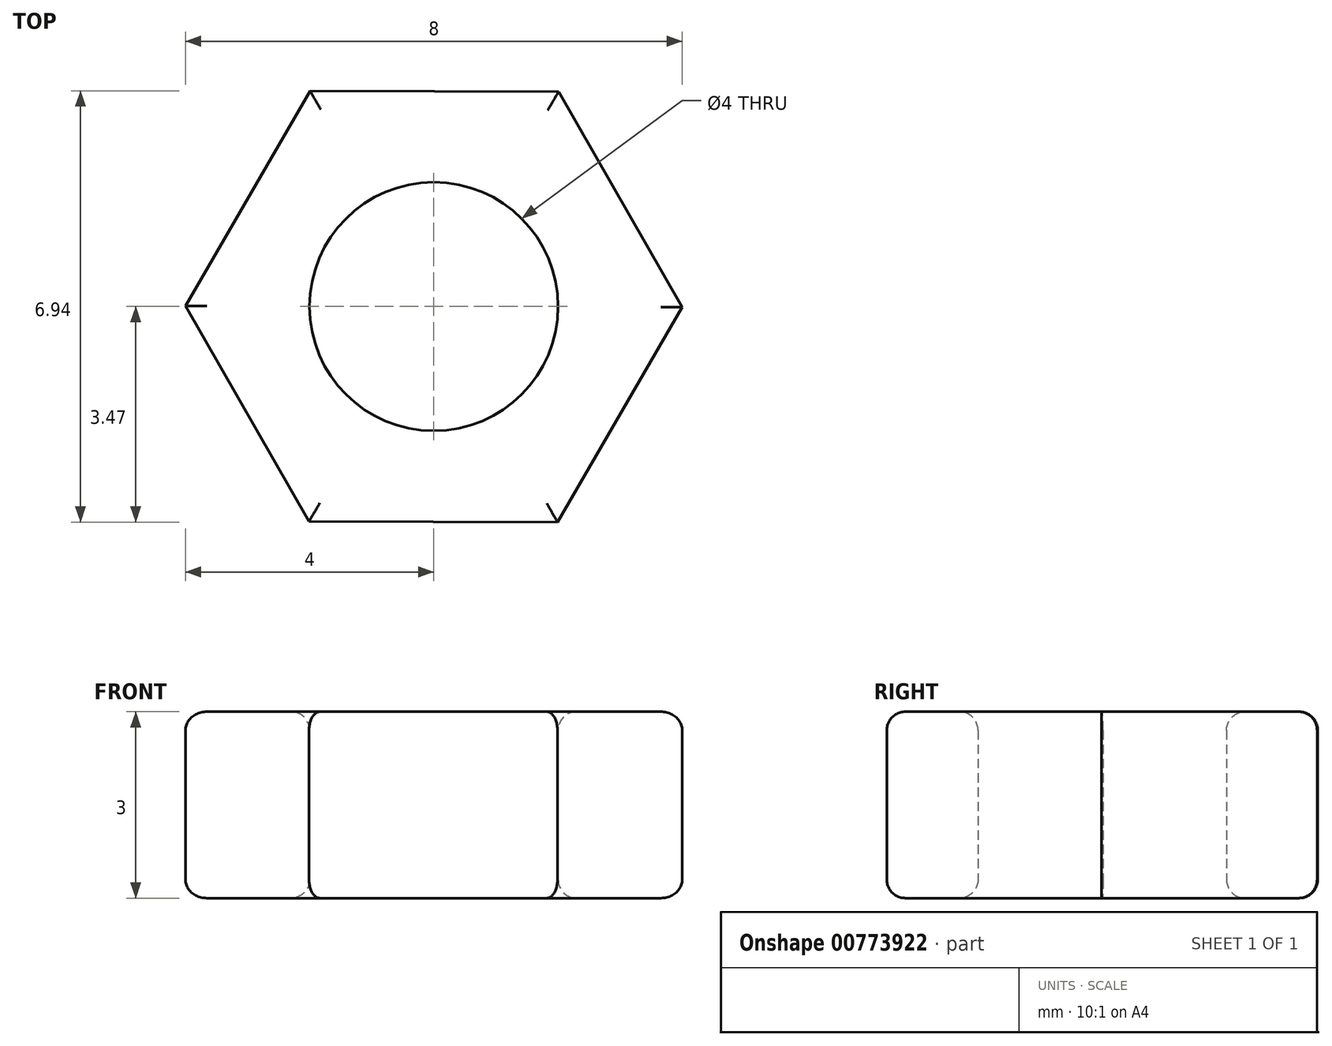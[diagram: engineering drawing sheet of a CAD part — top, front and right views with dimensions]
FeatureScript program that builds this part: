
annotation { "Feature Type Name" : "Feature", "Feature Type Description" : "" }
export const myFeature = defineFeature(function(context is Context, id is Id, definition is map)
    precondition{}
    {
        {
            var Q0;
            Q0=qCreatedBy(makeId("Top.planeOp"),FACE);
            var sketch = newSketch(context, id + "F0", { "sketchPlane" : qUnion([Q0])});
            skCircle(sketch, "E0.cCircle", {"center": v(0, 0) * mm, "radius": 4 * mm, "construction": true});
            skLineSegment(sketch, "E0.0", {"start": v(2, 3.46) * mm, "end": v(4, -0.01) * mm});
            skLineSegment(sketch, "E0.1", {"start": v(4, -0.01) * mm, "end": v(2, -3.47) * mm});
            skLineSegment(sketch, "E0.2", {"start": v(2, -3.47) * mm, "end": v(-2, -3.46) * mm});
            skLineSegment(sketch, "E0.3", {"start": v(-2, -3.46) * mm, "end": v(-4, 0.01) * mm});
            skLineSegment(sketch, "E0.4", {"start": v(-4, 0.01) * mm, "end": v(-2, 3.47) * mm});
            skLineSegment(sketch, "E0.5", {"start": v(-2, 3.47) * mm, "end": v(2, 3.46) * mm});
            skCircle(sketch, "E1", {"center": v(0, 0) * mm, "radius": 2 * mm});
            skSolve(sketch);
        }
        {
            var Q0;
            Q0 = qSketchRegion(id + "F0", true);
            extrude(context, id + "F1", {"entities" : qUnion([Q0]), "depth" : 3 * mm, "offsetDistance" : 25 * mm});
        }
        {
            var Q0;
            Q0=makeQuery(id+"F1.opExtrude","CAP_FACE",FACE,{"disambiguationData":[OSD([sQuery(id+"F0.wireOp",EDGE,"E0.0"),sQuery(id+"F0.wireOp",EDGE,"E0.1"),sQuery(id+"F0.wireOp",EDGE,"E0.2"),sQuery(id+"F0.wireOp",EDGE,"E0.3"),sQuery(id+"F0.wireOp",EDGE,"E0.4"),sQuery(id+"F0.wireOp",EDGE,"E0.5"),sQuery(id+"F0.wireOp",EDGE,"E1")])],"isStart":false});
            fillet(context, id + "F2", {"entities" : qUnion([Q0]), "radius" : 0.3 * mm, "tangentPropagation" : true, "allowEdgeOverflow" : false});
        }
        {
            var Q0;
            Q0=makeQuery(id+"F1.opExtrude","CAP_FACE",FACE,{"disambiguationData":[OSD([sQuery(id+"F0.wireOp",EDGE,"E0.0"),sQuery(id+"F0.wireOp",EDGE,"E0.1"),sQuery(id+"F0.wireOp",EDGE,"E0.2"),sQuery(id+"F0.wireOp",EDGE,"E0.3"),sQuery(id+"F0.wireOp",EDGE,"E0.4"),sQuery(id+"F0.wireOp",EDGE,"E0.5"),sQuery(id+"F0.wireOp",EDGE,"E1")])],"isStart":true});
            fillet(context, id + "F3", {"entities" : qUnion([Q0]), "radius" : 0.3 * mm, "tangentPropagation" : true, "allowEdgeOverflow" : false});
        }
    });
